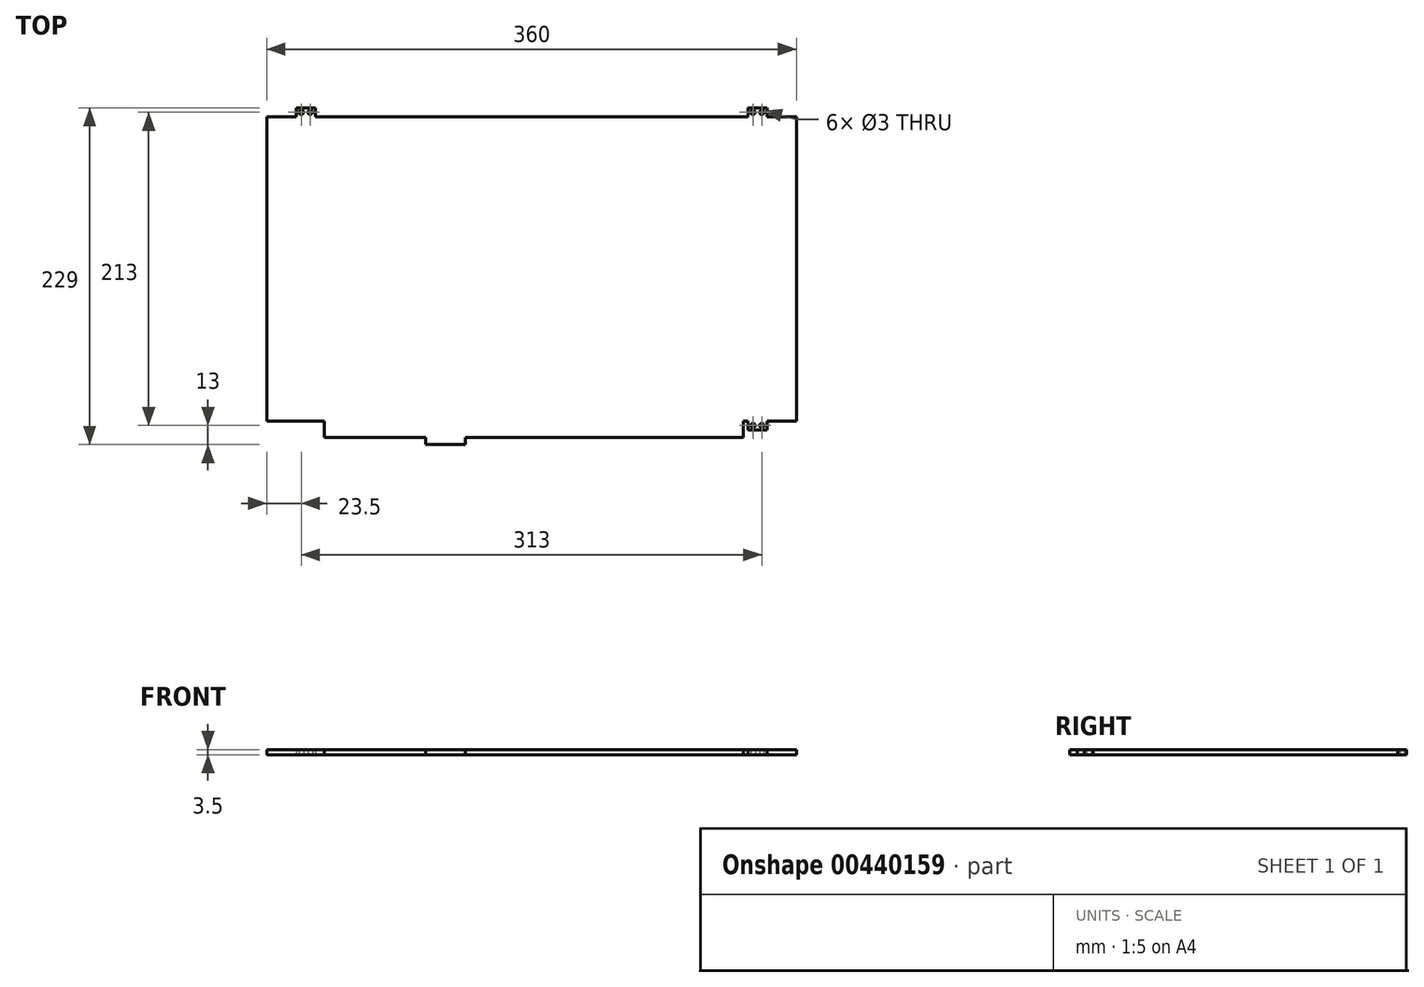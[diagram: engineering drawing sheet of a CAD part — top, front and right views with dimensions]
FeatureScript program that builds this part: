
annotation { "Feature Type Name" : "Feature", "Feature Type Description" : "" }
export const myFeature = defineFeature(function(context is Context, id is Id, definition is map)
    precondition{}
    {
        {
            var Q0;
            Q0=qCreatedBy(makeId("Top.planeOp"),FACE);
            var sketch = newSketch(context, id + "F0", { "sketchPlane" : qUnion([Q0])});
            skLineSegment(sketch, "E0.bottom", {"start": v(-180, 103.5) * mm, "end": v(-160, 103.5) * mm});
            skLineSegment(sketch, "E0.top", {"start": v(-180, -103.5) * mm, "end": v(-141, -103.5) * mm});
            skLineSegment(sketch, "E0.left", {"start": v(-180, 103.5) * mm, "end": v(-180, -103.5) * mm});
            skLineSegment(sketch, "E0.right", {"start": v(180, 103.5) * mm, "end": v(180, -103.5) * mm});
            skLineSegment(sketch, "E1.bottom", {"start": v(-160, 109.5) * mm, "end": v(-147, 109.5) * mm});
            skLineSegment(sketch, "E1.left", {"start": v(-160, 109.5) * mm, "end": v(-160, 103.5) * mm});
            skLineSegment(sketch, "E1.right", {"start": v(-147, 109.5) * mm, "end": v(-147, 103.5) * mm});
            skLineSegment(sketch, "E2.bottom", {"start": v(147, 109.5) * mm, "end": v(160, 109.5) * mm});
            skLineSegment(sketch, "E2.left", {"start": v(160, 109.5) * mm, "end": v(160, 103.5) * mm});
            skLineSegment(sketch, "E2.right", {"start": v(147, 109.5) * mm, "end": v(147, 103.5) * mm});
            skCircle(sketch, "E3", {"center": v(-156.5, 106.5) * mm, "radius": 1.5 * mm});
            skCircle(sketch, "E4", {"center": v(-150.5, 106.5) * mm, "radius": 1.5 * mm});
            skPoint(sketch, "E5", {"position": v(0, 103.5) * mm});
            skPoint(sketch, "E6", {"position": v(180, 0) * mm});
            skLineSegment(sketch, "E7.trimOffspring", {"start": v(-147, 103.5) * mm, "end": v(147, 103.5) * mm});
            skCircle(sketch, "E8", {"center": v(150.5, 106.5) * mm, "radius": 1.5 * mm});
            skCircle(sketch, "E9", {"center": v(156.5, 106.5) * mm, "radius": 1.5 * mm});
            skLineSegment(sketch, "E10.trimOffspring", {"start": v(160, 103.5) * mm, "end": v(180, 103.5) * mm});
            skLineSegment(sketch, "E11.top", {"start": v(147, -109.5) * mm, "end": v(160, -109.5) * mm});
            skLineSegment(sketch, "E11.left", {"start": v(147, -103.5) * mm, "end": v(147, -109.5) * mm});
            skLineSegment(sketch, "E11.right", {"start": v(160, -103.5) * mm, "end": v(160, -109.5) * mm});
            skCircle(sketch, "E12", {"center": v(150.5, -106.5) * mm, "radius": 1.5 * mm});
            skCircle(sketch, "E13", {"center": v(156.5, -106.5) * mm, "radius": 1.5 * mm});
            skLineSegment(sketch, "E14.trimOffspring", {"start": v(160, -103.5) * mm, "end": v(180, -103.5) * mm});
            skLineSegment(sketch, "E15.top", {"start": v(-141, -114.5) * mm, "end": v(144, -114.5) * mm});
            skLineSegment(sketch, "E15.left", {"start": v(-141, -103.5) * mm, "end": v(-141, -114.5) * mm});
            skLineSegment(sketch, "E15.right", {"start": v(144, -103.5) * mm, "end": v(144, -114.5) * mm});
            skLineSegment(sketch, "E16.trimOffspring", {"start": v(144, -103.5) * mm, "end": v(147, -103.5) * mm});
            skLineSegment(sketch, "E17.bottom", {"start": v(-72, -114.5) * mm, "end": v(-45, -114.5) * mm});
            skLineSegment(sketch, "E17.top", {"start": v(-72, -119.5) * mm, "end": v(-45, -119.5) * mm});
            skLineSegment(sketch, "E17.left", {"start": v(-72, -114.5) * mm, "end": v(-72, -119.5) * mm});
            skLineSegment(sketch, "E17.right", {"start": v(-45, -114.5) * mm, "end": v(-45, -119.5) * mm});
            skSolve(sketch);
        }
        {
            var Q0;
            Q0=makeQuery(id+"F0.imprint","IMPRINT",FACE,{"disambiguationData":[TD([[makeQuery(id+"F0.imprint","IMPRINT",EDGE,{"derivedFrom":sQuery(id+"F0.wireOp",EDGE,"E0.bottom")}),-1.0]])]});
            var sketch = newSketch(context, id + "F1", { "sketchPlane" : qUnion([Q0])});
            skLineSegment(sketch, "E18.bottom", {"start": v(-176.5, 100) * mm, "end": v(171.25, 100) * mm});
            skLineSegment(sketch, "E18.top", {"start": v(-176.5, -97.5) * mm, "end": v(171.25, -97.5) * mm});
            skLineSegment(sketch, "E18.left", {"start": v(-176.5, 100) * mm, "end": v(-176.5, -97.5) * mm});
            skLineSegment(sketch, "E18.right", {"start": v(171.25, 100) * mm, "end": v(171.25, -97.5) * mm});
            skSolve(sketch);
        }
        {
            var Q0;
            Q0 = qSketchRegion(id + "F0", true);
            extrude(context, id + "F2", {"entities" : qUnion([Q0]), "depth" : 3.5 * mm});
        }
    });
